FCSTD DOCUMENT  (FreeCAD 0.21R33694 (Git))
Label: kumiko_lattice_assembly
License: All rights reserved
LicenseURL: http://en.wikipedia.org/wiki/All_rights_reserved
objects: App::Link×9, App::Part×1
EXTERNAL_REF file=../master_kumiko_box.FCStd obj=Spreadsheet
EXTERNAL_REF file=../parts/kumiko/kumiko_strip_short.FCStd obj=Body052
EXTERNAL_REF file=../parts/kumiko/kumiko_strip_long.FCStd obj=Body053
EXTERNAL_REF file=../parts/kumiko/kumiko_strip_long_holes.FCStd obj=Body052
EXTERNAL_REF file=../parts/kumiko/kumiko_strip_short_holes.FCStd obj=Body052

FEATURE [App::Link] Link002  label="SpreadSheet"
  LinkedObject = -> <external ../master_kumiko_box.FCStd>#Spreadsheet
FEATURE [App::Link] Link003  label="short_strip_a"
  LinkPlacement = pos=(27.5,3,11) rot=(1,1,0;3.14159rad)
  LinkedObject = -> <external ../parts/kumiko/kumiko_strip_short.FCStd>#Body052
  Placement = pos=(27.5,3,11) rot=(1,1,0;3.14159rad)
  expr: .Placement.Base.x = <<SpreadSheet>>.kumiko_grid_size
  expr: .Placement.Base.y = <<SpreadSheet>>.kumiko_thickness
  expr: .Placement.Base.z = <<SpreadSheet>>.kumiko_hight
  expr: .Placement.Rotation.Angle = 180
  expr: .Placement.Rotation.Axis.x = 1
  expr: .Placement.Rotation.Axis.y = 1
  expr: .Placement.Rotation.Axis.z = 0
FEATURE [App::Link] Link004  label="short_strip_b"
  LinkPlacement = pos=(55,3,11) rot=(1,1,0;3.14159rad)
  LinkedObject = -> <external ../parts/kumiko/kumiko_strip_short.FCStd>#Body052
  Placement = pos=(55,3,11) rot=(1,1,0;3.14159rad)
  expr: .Placement.Base.x = <<SpreadSheet>>.kumiko_grid_size * 2
  expr: .Placement.Base.y = <<SpreadSheet>>.kumiko_thickness
  expr: .Placement.Base.z = <<SpreadSheet>>.kumiko_hight
  expr: .Placement.Rotation.Angle = 180
  expr: .Placement.Rotation.Axis.x = 1
  expr: .Placement.Rotation.Axis.y = 1
  expr: .Placement.Rotation.Axis.z = 0
FEATURE [App::Link] Link005  label="short_strip_c"
  LinkPlacement = pos=(82.5,3,11) rot=(1,1,0;3.14159rad)
  LinkedObject = -> <external ../parts/kumiko/kumiko_strip_short.FCStd>#Body052
  Placement = pos=(82.5,3,11) rot=(1,1,0;3.14159rad)
  expr: .Placement.Base.x = <<SpreadSheet>>.kumiko_grid_size * 3
  expr: .Placement.Base.y = <<SpreadSheet>>.kumiko_thickness
  expr: .Placement.Base.z = <<SpreadSheet>>.kumiko_hight
  expr: .Placement.Rotation.Angle = 180
  expr: .Placement.Rotation.Axis.x = 1
  expr: .Placement.Rotation.Axis.y = 1
  expr: .Placement.Rotation.Axis.z = 0
FEATURE [App::Link] Link009  label="strip_long_center"
  LinkPlacement = pos=(3,27.5,0) rot=(0,0,1;0rad)
  LinkedObject = -> <external ../parts/kumiko/kumiko_strip_long.FCStd>#Body053
  Placement = pos=(3,27.5,0) rot=(0,0,1;0rad)
  expr: .Placement.Base.x = <<SpreadSheet>>.kumiko_thickness
  expr: .Placement.Base.y = <<SpreadSheet>>.kumiko_grid_size
FEATURE [App::Link] Link  label="strip_long_front"
  LinkPlacement = pos=(3,0,0) rot=(0,0,1;0rad)
  LinkedObject = -> <external ../parts/kumiko/kumiko_strip_long_holes.FCStd>#Body052
  Placement = pos=(3,0,0) rot=(0,0,1;0rad)
  expr: .Placement.Base.x = <<SpreadSheet>>.kumiko_thickness
FEATURE [App::Link] Link010  label="strip_long_back"
  LinkPlacement = pos=(3,55,0) rot=(0,0,1;0rad)
  LinkedObject = -> <external ../parts/kumiko/kumiko_strip_long_holes.FCStd>#Body052
  Placement = pos=(3,55,0) rot=(0,0,1;0rad)
  expr: .Placement.Base.x = <<SpreadSheet>>.kumiko_thickness
  expr: .Placement.Base.y = <<SpreadSheet>>.kumiko_grid_size * 2
FEATURE [App::Link] Link011  label="short_strip_left"
  LinkPlacement = pos=(0,0,11) rot=(1,1,0;3.14159rad)
  LinkedObject = -> <external ../parts/kumiko/kumiko_strip_short_holes.FCStd>#Body052
  Placement = pos=(0,0,11) rot=(1,1,0;3.14159rad)
  expr: .Placement.Base.y = 0
  expr: .Placement.Base.z = <<SpreadSheet>>.kumiko_hight
FEATURE [App::Link] Link012  label="short_strip_right"
  LinkPlacement = pos=(110,0,11) rot=(1,1,0;3.14159rad)
  LinkedObject = -> <external ../parts/kumiko/kumiko_strip_short_holes.FCStd>#Body052
  Placement = pos=(110,0,11) rot=(1,1,0;3.14159rad)
  expr: .Placement.Base.x = <<SpreadSheet>>.kumiko_grid_size * 4
  expr: .Placement.Base.y = 0
  expr: .Placement.Base.z = <<SpreadSheet>>.kumiko_hight
FEATURE [App::Part] Part  label="lattice"
  Group = -> [Link005,Link,Link003,Link009,Link004,Link010,Link011,Link012]
  Origin = -> Origin

RESOLVED EXTERNAL PARTS (link-assembly join: the EXTERNAL_REF files above that resolve inside this repo's crawl, each included once):
---- part ../master_kumiko_box.FCStd = doc fcstd_d57fc246fb5e ----
FCSTD DOCUMENT  (FreeCAD 0.21R33771 (Git))
Label: master_kumiko_box
License: All rights reserved
LicenseURL: https://en.wikipedia.org/wiki/All_rights_reserved
objects: App::Link×3, App::Part×2, Spreadsheet::Sheet×1
EXTERNAL_REF file=assembly/box_assembly.FCStd obj=Part
EXTERNAL_REF file=assembly/lid_assembly.FCStd obj=Part
EXTERNAL_REF file=assembly/kumiko_assembly.FCStd obj=Part001

FEATURE [Spreadsheet::Sheet] Spreadsheet  label="SpreadSheet"
  cells = A1='name; B1='value; C1='calc (y/n); A2='box_length; B2(box_length)=130; C2='n; A3='box_width; B3(box_width)==B2 / 2 + B5 - B13 / 2; C3='n; A4='box_height; B4(box_height)=60; C4='y; A5='box_thickness; B5(box_thickness)=11.5; C5='y; A7='lid_height; B7(lid_height)==B8 * 17 / 8.5; C7='y; A8='lid_frame_width; B8(lid_frame_width)==B5 - B13; C8='y; A9='lid_lip_width; B9(lid_lip_width)==B5 - B8; C9='y; A10='lid_lip_height; B10(lid_lip_hight)=3; C10='y; A12='kumiko_hight; B12(kumiko_hight)==B7 * 11 / 17; C12='y; A13='kumiko_thickness; B13(kumiko_thickness)=3; C13='n; A14='kumiko_grid_size; B14(kumiko_grid_size)==(B2 - 2 * B8 - B13) / 4; C14='y; A16='box_wall_height; B16(box_wall_height)==B4 - B7 - B18; C16='y; A18='floor_edge; B18(floor_edge)=2; C18='n; A20='cnc_spacing; B20(cnc_spacing)=0; C20='y
FEATURE [App::Link] Link  label="box"
  LinkedObject = -> <external assembly/box_assembly.FCStd>#Part
FEATURE [App::Link] Link001  label="lid"
  LinkPlacement = pos=(0,0,43) rot=(0,0,1;0rad)
  LinkedObject = -> <external assembly/lid_assembly.FCStd>#Part
  Placement = pos=(0,0,43) rot=(0,0,1;0rad)
  expr: .Placement.Base.z = <<SpreadSheet>>.box_height - <<SpreadSheet>>.lid_height
FEATURE [App::Link] Link002  label="kumiko_assembly"
  LinkPlacement = pos=(8.5,8.5,49) rot=(0,0,1;0rad)
  LinkedObject = -> <external assembly/kumiko_assembly.FCStd>#Part001
  Placement = pos=(8.5,8.5,49) rot=(0,0,1;0rad)
  expr: .Placement.Base.x = <<SpreadSheet>>.lid_frame_width
  expr: .Placement.Base.y = <<SpreadSheet>>.lid_frame_width
  expr: .Placement.Base.z = <<SpreadSheet>>.box_height - Spreadsheet.kumiko_hight
FEATURE [App::Part] Part  label="lid_complete"
  Group = -> [Link002,Link001]
  Origin = -> Origin
FEATURE [App::Part] Part001  label="kumiko_box_complete"
  Group = -> [Part,Link]
  Origin = -> Origin001
---- part ../parts/kumiko/kumiko_strip_long.FCStd = doc fcstd_fbc0481b5c11 ----
FCSTD DOCUMENT  (FreeCAD 0.21R33694 (Git))
Label: kumiko_strip_long
License: All rights reserved
LicenseURL: https://en.wikipedia.org/wiki/All_rights_reserved
objects: Sketcher::SketchObject×3, PartDesign::Pad×2, PartDesign::LinearPattern×2, App::Link×1, PartDesign::Pocket×1, PartDesign::Body×1
note: 12 computed .brp shape members not serialized (recipe doc carries the construction recipe); baked Part::Feature solids carry a one-line shape summary decoded from their .brp
EXTERNAL_REF file=../../master_kumiko_box.FCStd obj=Spreadsheet

FEATURE [App::Link] Link  label="SpreadSheet"
  LinkedObject = -> <external ../../master_kumiko_box.FCStd>#Spreadsheet
FEATURE [Sketcher::SketchObject] Sketch081  label="strip_profile_drawing001"
  FullyConstrained = true
  MapMode = 5
  Placement = pos=(0,0,0) rot=(0.57735,0.57735,0.57735;2.0944rad)
  Support = -> [YZ_Plane071]
  expr: Constraints[10] = 0
  expr: Constraints[8] = <<SpreadSheet>>.kumiko_thickness
  expr: Constraints[9] = <<SpreadSheet>>.kumiko_hight
  sketch-geometry (4):
    g0: LineSegment StartX=0 StartY=11 StartZ=0 EndX=3 EndY=11 EndZ=0
    g1: LineSegment StartX=3 StartY=11 StartZ=0 EndX=3 EndY=0 EndZ=0
    g2: LineSegment StartX=3 StartY=0 StartZ=0 EndX=0 EndY=0 EndZ=0
    g3: LineSegment StartX=0 StartY=0 StartZ=0 EndX=0 EndY=11 EndZ=0
  constraints (12):
    c: Coincident(g0,g1)
    c: Coincident(g1,g2)
    c: Coincident(g2,g3)
    c: Coincident(g3,g0)
    c: Horizontal(g0)
    c: Horizontal(g2)
    c: Vertical(g1)
    c: Vertical(g3)
    c: DistanceX(g0,g0) = 3
    c: DistanceY(g3,g3) = 11
    c: DistanceX(g0,g-1) = 0
    c: DistanceY(g-1,g2) = 0
FEATURE [PartDesign::Pad] Pad038  label="strip_extrusion001"
  Direction = (1,-2e-16,3e-16)
  Length = 107
  Length2 = 10
  Placement = pos=(0,0,0) rot=(0.57735,0.57735,0.57735;2.0944rad)
  Profile = -> Sketch081
  ReferenceAxis = -> Sketch081 [N_Axis]
  Type = 0
  expr: Length = <<SpreadSheet>>.box_length - 2 * <<SpreadSheet>>.lid_frame_width - 2 * <<SpreadSheet>>.kumiko_thickness
FEATURE [Sketcher::SketchObject] Sketch
  FullyConstrained = true
  MapMode = 5
  Placement = pos=(107,-2.35e-14,2.35e-14) rot=(0.57735,0.57735,0.57735;2.0944rad)
  Support = -> [Pad038]
  expr: Constraints[0] = <<SpreadSheet>>.kumiko_thickness / 2
  expr: Constraints[12] = <<SpreadSheet>>.kumiko_thickness
  expr: Constraints[1] = <<SpreadSheet>>.kumiko_hight / 2
  sketch-geometry (5):
    g0: GeomPoint X=1.5 Y=5.5 Z=0
    g1: LineSegment StartX=0 StartY=7 StartZ=0 EndX=3 EndY=7 EndZ=0
    g2: LineSegment StartX=3 StartY=7 StartZ=0 EndX=3 EndY=4 EndZ=0
    g3: LineSegment StartX=3 StartY=4 StartZ=0 EndX=0 EndY=4 EndZ=0
    g4: LineSegment StartX=0 StartY=4 StartZ=0 EndX=0 EndY=7 EndZ=0
  constraints (13):
    c: DistanceX(g-1,g0) = 1.5
    c: DistanceY(g-1,g0) = 5.5
    c: Coincident(g1,g2)
    c: Coincident(g2,g3)
    c: Coincident(g3,g4)
    c: Coincident(g4,g1)
    c: Horizontal(g1)
    c: Horizontal(g3)
    c: Vertical(g2)
    c: Vertical(g4)
    c: Symmetric(g1,g2,g0)
    c: Equal(g4,g1)
    c: DistanceY(g2,g2) = 3
FEATURE [PartDesign::Pad] Pad
  BaseFeature = -> Pad038
  Direction = (1,-4e-16,4e-16)
  Length = 6
  Length2 = 10
  Placement = pos=(0,0,0) rot=(0.57735,0.57735,0.57735;2.0944rad)
  Profile = -> Sketch
  ReferenceAxis = -> Sketch [N_Axis]
  Type = 0
  expr: Length = <<SpreadSheet>>.kumiko_thickness * 2
FEATURE [PartDesign::LinearPattern] LinearPattern001
  BaseFeature = -> Pad
  Direction = -> X_Axis071
  Length = 113
  Occurrences = 2
  Originals = -> [Pad]
  Placement = pos=(0,0,0) rot=(0.57735,0.57735,0.57735;2.0944rad)
  Reversed = true
  expr: Length = <<SpreadSheet>>.box_length - 2 * <<SpreadSheet>>.lid_frame_width
FEATURE [Sketcher::SketchObject] Sketch082
  FullyConstrained = true
  MapMode = 5
  Placement = pos=(0,0,0) rot=(-0.57735,-0.57735,0.57735;4.18879rad)
  Support = -> [LinearPattern001]
  expr: Constraints[0] = <<SpreadSheet>>.kumiko_hight / 2
  expr: Constraints[10] = <<SpreadSheet>>.kumiko_thickness
  expr: Constraints[12] = -<<SpreadSheet>>.kumiko_hight / 2
  expr: Constraints[1] = <<SpreadSheet>>.kumiko_grid_size - <<SpreadSheet>>.kumiko_thickness / 2
  sketch-geometry (5):
    g0: GeomPoint X=-5.5 Y=26 Z=0
    g1: LineSegment StartX=-5.5 StartY=27.5 StartZ=0 EndX=-11 EndY=27.5 EndZ=0
    g2: LineSegment StartX=-11 StartY=27.5 StartZ=0 EndX=-11 EndY=24.5 EndZ=0
    g3: LineSegment StartX=-11 StartY=24.5 StartZ=0 EndX=-5.5 EndY=24.5 EndZ=0
    g4: LineSegment StartX=-5.5 StartY=24.5 StartZ=0 EndX=-5.5 EndY=27.5 EndZ=0
  constraints (13):
    c: DistanceX(g0,g-1) = 5.5
    c: DistanceY(g-1,g0) = 26
    c: Coincident(g1,g2)
    c: Coincident(g2,g3)
    c: Coincident(g3,g4)
    c: Coincident(g4,g1)
    c: Horizontal(g1)
    c: Horizontal(g3)
    c: Vertical(g2)
    c: Vertical(g4)
    c: DistanceY(g2,g2) = 3
    c: Symmetric(g1,g3,g0)
    c: DistanceX(g1,g1) = -5.5
FEATURE [PartDesign::Pocket] Pocket
  BaseFeature = -> LinearPattern001
  Direction = (7e-16,1,-4e-16)
  Length = 3
  Length2 = 5
  Placement = pos=(0,0,0) rot=(0.57735,0.57735,0.57735;2.0944rad)
  Profile = -> Sketch082
  ReferenceAxis = -> Sketch082 [N_Axis]
  Type = 0
  expr: Length = <<SpreadSheet>>.kumiko_thickness
FEATURE [PartDesign::LinearPattern] LinearPattern002
  BaseFeature = -> Pocket
  Direction = -> X_Axis071
  Length = 55
  Occurrences = 3
  Originals = -> [Pocket]
  Placement = pos=(0,0,0) rot=(0.57735,0.57735,0.57735;2.0944rad)
  expr: Length = <<SpreadSheet>>.kumiko_grid_size * 2
FEATURE [PartDesign::Body] Body053  label="strip_long_body001"
  Group = -> [Sketch081,Pad038,Sketch,Pad,LinearPattern001,Sketch082,Pocket,LinearPattern002]
  Origin = -> Origin071
  Tip = -> LinearPattern002
  expr: .Placement.Base.x = 0
  expr: .Placement.Base.y = 0
  expr: .Placement.Base.z = 0
---- part ../parts/kumiko/kumiko_strip_long_holes.FCStd = doc fcstd_25b771c1c85f ----
FCSTD DOCUMENT  (FreeCAD 0.21R33694 (Git))
Label: kumiko_strip_long_holes
License: All rights reserved
LicenseURL: http://en.wikipedia.org/wiki/All_rights_reserved
objects: Sketcher::SketchObject×3, PartDesign::Pad×2, PartDesign::LinearPattern×2, App::Link×1, PartDesign::Pocket×1, PartDesign::Body×1
note: 12 computed .brp shape members not serialized (recipe doc carries the construction recipe); baked Part::Feature solids carry a one-line shape summary decoded from their .brp
EXTERNAL_REF file=../../master_kumiko_box.FCStd obj=Spreadsheet

FEATURE [App::Link] Link  label="SpreadSheet"
  LinkedObject = -> <external ../../master_kumiko_box.FCStd>#Spreadsheet
FEATURE [Sketcher::SketchObject] Sketch079  label="strip_profile_drawing"
  FullyConstrained = true
  MapMode = 5
  Placement = pos=(0,0,0) rot=(0.57735,0.57735,0.57735;2.0944rad)
  Support = -> [YZ_Plane070]
  expr: Constraints[10] = 0
  expr: Constraints[8] = <<SpreadSheet>>.kumiko_thickness
  expr: Constraints[9] = <<SpreadSheet>>.kumiko_hight
  sketch-geometry (4):
    g0: LineSegment StartX=0 StartY=11 StartZ=0 EndX=3 EndY=11 EndZ=0
    g1: LineSegment StartX=3 StartY=11 StartZ=0 EndX=3 EndY=0 EndZ=0
    g2: LineSegment StartX=3 StartY=0 StartZ=0 EndX=0 EndY=0 EndZ=0
    g3: LineSegment StartX=0 StartY=0 StartZ=0 EndX=0 EndY=11 EndZ=0
  constraints (12):
    c: Coincident(g0,g1)
    c: Coincident(g1,g2)
    c: Coincident(g2,g3)
    c: Coincident(g3,g0)
    c: Horizontal(g0)
    c: Horizontal(g2)
    c: Vertical(g1)
    c: Vertical(g3)
    c: DistanceX(g0,g0) = 3
    c: DistanceY(g3,g3) = 11
    c: DistanceX(g0,g-1) = 0
    c: DistanceY(g-1,g2) = 0
FEATURE [PartDesign::Pad] Pad037  label="strip_extrusion"
  Direction = (1,-2e-16,3e-16)
  Length = 107
  Length2 = 10
  Placement = pos=(0,0,0) rot=(0.57735,0.57735,0.57735;2.0944rad)
  Profile = -> Sketch079
  ReferenceAxis = -> Sketch079 [N_Axis]
  Type = 0
  expr: Length = <<SpreadSheet>>.box_length - 2 * <<SpreadSheet>>.lid_frame_width - 2 * <<SpreadSheet>>.kumiko_thickness
FEATURE [Sketcher::SketchObject] Sketch
  FullyConstrained = true
  MapMode = 5
  Placement = pos=(107,-2.35e-14,2.35e-14) rot=(0.57735,0.57735,0.57735;2.0944rad)
  Support = -> [Pad037]
  expr: Constraints[0] = <<SpreadSheet>>.kumiko_thickness / 2
  expr: Constraints[12] = <<SpreadSheet>>.kumiko_thickness
  expr: Constraints[1] = <<SpreadSheet>>.kumiko_hight / 2
  sketch-geometry (5):
    g0: GeomPoint X=1.5 Y=5.5 Z=0
    g1: LineSegment StartX=0 StartY=7 StartZ=0 EndX=3 EndY=7 EndZ=0
    g2: LineSegment StartX=3 StartY=7 StartZ=0 EndX=3 EndY=4 EndZ=0
    g3: LineSegment StartX=3 StartY=4 StartZ=0 EndX=0 EndY=4 EndZ=0
    g4: LineSegment StartX=0 StartY=4 StartZ=0 EndX=0 EndY=7 EndZ=0
  constraints (13):
    c: DistanceX(g-1,g0) = 1.5
    c: DistanceY(g-1,g0) = 5.5
    c: Coincident(g1,g2)
    c: Coincident(g2,g3)
    c: Coincident(g3,g4)
    c: Coincident(g4,g1)
    c: Horizontal(g1)
    c: Horizontal(g3)
    c: Vertical(g2)
    c: Vertical(g4)
    c: Symmetric(g1,g2,g0)
    c: Equal(g4,g1)
    c: DistanceY(g2,g2) = 3
FEATURE [PartDesign::Pad] Pad
  BaseFeature = -> Pad037
  Direction = (1,-4e-16,4e-16)
  Length = 3
  Length2 = 10
  Placement = pos=(0,0,0) rot=(0.57735,0.57735,0.57735;2.0944rad)
  Profile = -> Sketch
  ReferenceAxis = -> Sketch [N_Axis]
  Type = 0
  expr: Length = <<SpreadSheet>>.kumiko_thickness
FEATURE [PartDesign::LinearPattern] LinearPattern
  BaseFeature = -> Pad
  Direction = -> X_Axis070
  Length = 110
  Occurrences = 2
  Originals = -> [Pad]
  Placement = pos=(0,0,0) rot=(0.57735,0.57735,0.57735;2.0944rad)
  Reversed = true
  expr: Length = <<SpreadSheet>>.box_length - 2 * <<SpreadSheet>>.lid_frame_width - <<SpreadSheet>>.kumiko_thickness
FEATURE [Sketcher::SketchObject] Sketch080
  FullyConstrained = true
  MapMode = 5
  Placement = pos=(0,0,0) rot=(-0.57735,-0.57735,0.57735;4.18879rad)
  Support = -> [LinearPattern]
  expr: Constraints[0] = <<SpreadSheet>>.kumiko_hight / 2
  expr: Constraints[12] = <<SpreadSheet>>.kumiko_thickness
  expr: Constraints[1] = <<SpreadSheet>>.kumiko_grid_size - <<SpreadSheet>>.kumiko_thickness / 2
  sketch-geometry (5):
    g0: GeomPoint X=-5.5 Y=26 Z=0
    g1: LineSegment StartX=-7 StartY=27.5 StartZ=0 EndX=-4 EndY=27.5 EndZ=0
    g2: LineSegment StartX=-4 StartY=27.5 StartZ=0 EndX=-4 EndY=24.5 EndZ=0
    g3: LineSegment StartX=-4 StartY=24.5 StartZ=0 EndX=-7 EndY=24.5 EndZ=0
    g4: LineSegment StartX=-7 StartY=24.5 StartZ=0 EndX=-7 EndY=27.5 EndZ=0
  constraints (13):
    c: DistanceX(g0,g-1) = 5.5
    c: DistanceY(g-1,g0) = 26
    c: Coincident(g1,g2)
    c: Coincident(g2,g3)
    c: Coincident(g3,g4)
    c: Coincident(g4,g1)
    c: Horizontal(g1)
    c: Horizontal(g3)
    c: Vertical(g2)
    c: Vertical(g4)
    c: Symmetric(g1,g2,g0)
    c: Equal(g1,g4)
    c: DistanceY(g2,g2) = 3
FEATURE [PartDesign::Pocket] Pocket
  BaseFeature = -> LinearPattern
  Direction = (7e-16,1,-4e-16)
  Length = 3
  Length2 = 5
  Placement = pos=(0,0,0) rot=(0.57735,0.57735,0.57735;2.0944rad)
  Profile = -> Sketch080
  ReferenceAxis = -> Sketch080 [N_Axis]
  Type = 0
  expr: Length = <<SpreadSheet>>.kumiko_thickness
FEATURE [PartDesign::LinearPattern] LinearPattern001
  BaseFeature = -> Pocket
  Direction = -> X_Axis070
  Length = 55
  Occurrences = 3
  Originals = -> [Pocket]
  Placement = pos=(0,0,0) rot=(0.57735,0.57735,0.57735;2.0944rad)
  expr: Length = <<SpreadSheet>>.kumiko_grid_size * 2
FEATURE [PartDesign::Body] Body052  label="strip_long_body"
  Group = -> [Sketch079,Pad037,Sketch,Pad,LinearPattern,Sketch080,Pocket,LinearPattern001]
  Origin = -> Origin070
  Tip = -> LinearPattern001
  expr: .Placement.Base.x = 0
  expr: .Placement.Base.y = 0
  expr: .Placement.Base.z = 0
---- part ../parts/kumiko/kumiko_strip_short.FCStd = doc fcstd_705df1ea343c ----
FCSTD DOCUMENT  (FreeCAD 0.21R33694 (Git))
Label: kumiko_strip_short
License: All rights reserved
LicenseURL: https://en.wikipedia.org/wiki/All_rights_reserved
objects: Sketcher::SketchObject×3, PartDesign::Pad×2, PartDesign::Pocket×1, App::Link×1, PartDesign::LinearPattern×1, PartDesign::Body×1
note: 11 computed .brp shape members not serialized (recipe doc carries the construction recipe); baked Part::Feature solids carry a one-line shape summary decoded from their .brp
EXTERNAL_REF file=../../master_kumiko_box.FCStd obj=Spreadsheet

FEATURE [Sketcher::SketchObject] Sketch079  label="short_strip_profile"
  FullyConstrained = true
  MapMode = 5
  Placement = pos=(0,0,0) rot=(0.57735,0.57735,0.57735;2.0944rad)
  Support = -> [YZ_Plane070]
  expr: Constraints[10] = 0
  expr: Constraints[8] = <<SpreadSheet>>.kumiko_thickness
  expr: Constraints[9] = <<SpreadSheet>>.kumiko_hight
  sketch-geometry (4):
    g0: LineSegment StartX=0 StartY=11 StartZ=0 EndX=3 EndY=11 EndZ=0
    g1: LineSegment StartX=3 StartY=11 StartZ=0 EndX=3 EndY=0 EndZ=0
    g2: LineSegment StartX=3 StartY=0 StartZ=0 EndX=0 EndY=0 EndZ=0
    g3: LineSegment StartX=0 StartY=0 StartZ=0 EndX=0 EndY=11 EndZ=0
  constraints (12):
    c: Coincident(g0,g1)
    c: Coincident(g1,g2)
    c: Coincident(g2,g3)
    c: Coincident(g3,g0)
    c: Horizontal(g0)
    c: Horizontal(g2)
    c: Vertical(g1)
    c: Vertical(g3)
    c: DistanceX(g0,g0) = 3
    c: DistanceY(g3,g3) = 11
    c: DistanceX(g0,g-1) = 0
    c: DistanceY(g-1,g2) = 0
FEATURE [PartDesign::Pad] Pad037  label="short_strip_extrusion"
  Direction = (1,-2e-16,3e-16)
  Length = 52
  Length2 = 10
  Placement = pos=(0,0,0) rot=(0.57735,0.57735,0.57735;2.0944rad)
  Profile = -> Sketch079
  ReferenceAxis = -> Sketch079 [N_Axis]
  Type = 0
  expr: Length = <<SpreadSheet>>.box_width - 2 * <<SpreadSheet>>.lid_frame_width - 2 * <<SpreadSheet>>.kumiko_thickness
FEATURE [Sketcher::SketchObject] Sketch080  label="half_lap_drawing"
  FullyConstrained = true
  MapMode = 5
  Placement = pos=(0,0,0) rot=(-0.57735,-0.57735,0.57735;4.18879rad)
  Support = -> [Pad037]
  expr: Constraints[10] = (<<SpreadSheet>>.box_width - 2 * <<SpreadSheet>>.lid_frame_width - <<SpreadSheet>>.kumiko_thickness - 2 * <<SpreadSheet>>.kumiko_thickness) / 2
  expr: Constraints[11] = <<SpreadSheet>>.kumiko_hight / 2
  expr: Constraints[8] = <<SpreadSheet>>.kumiko_thickness
  expr: Constraints[9] = <<SpreadSheet>>.kumiko_hight / 2
  sketch-geometry (4):
    g0: LineSegment StartX=-11 StartY=24.5 StartZ=0 EndX=-5.5 EndY=24.5 EndZ=0
    g1: LineSegment StartX=-5.5 StartY=24.5 StartZ=0 EndX=-5.5 EndY=27.5 EndZ=0
    g2: LineSegment StartX=-5.5 StartY=27.5 StartZ=0 EndX=-11 EndY=27.5 EndZ=0
    g3: LineSegment StartX=-11 StartY=27.5 StartZ=0 EndX=-11 EndY=24.5 EndZ=0
  constraints (12):
    c: Coincident(g0,g1)
    c: Coincident(g1,g2)
    c: Coincident(g2,g3)
    c: Coincident(g3,g0)
    c: Horizontal(g0)
    c: Horizontal(g2)
    c: Vertical(g1)
    c: Vertical(g3)
    c: DistanceY(g1,g1) = 3
    c: DistanceX(g0,g0) = 5.5
    c: DistanceY(g-1,g0) = 24.5
    c: DistanceX(g0,g-1) = 5.5
FEATURE [PartDesign::Pocket] Pocket019  label="half_lap_joint"
  BaseFeature = -> Pad037
  Direction = (4e-16,1,-2e-16)
  Length = 3
  Length2 = 5
  Placement = pos=(0,0,0) rot=(0.57735,0.57735,0.57735;2.0944rad)
  Profile = -> Sketch080
  ReferenceAxis = -> Sketch080 [N_Axis]
  Type = 0
  expr: Length = <<SpreadSheet>>.kumiko_thickness
FEATURE [App::Link] Link  label="SpreadSheet"
  LinkedObject = -> <external ../../master_kumiko_box.FCStd>#Spreadsheet
FEATURE [Sketcher::SketchObject] Sketch
  FullyConstrained = true
  MapMode = 5
  Placement = pos=(52,-1.14e-14,1.14e-14) rot=(0.57735,0.57735,0.57735;2.0944rad)
  Support = -> [Pocket019]
  expr: Constraints[11] = <<SpreadSheet>>.kumiko_thickness
  expr: Constraints[8] = <<SpreadSheet>>.kumiko_thickness / 2
  expr: Constraints[9] = <<SpreadSheet>>.kumiko_hight / 2
  sketch-geometry (5):
    g0: LineSegment StartX=0 StartY=4 StartZ=0 EndX=3 EndY=4 EndZ=0
    g1: LineSegment StartX=3 StartY=4 StartZ=0 EndX=3 EndY=7 EndZ=0
    g2: LineSegment StartX=3 StartY=7 StartZ=0 EndX=0 EndY=7 EndZ=0
    g3: LineSegment StartX=0 StartY=7 StartZ=0 EndX=0 EndY=4 EndZ=0
    g4: GeomPoint X=1.5 Y=5.5 Z=0
  constraints (13):
    c: Coincident(g0,g1)
    c: Coincident(g1,g2)
    c: Coincident(g2,g3)
    c: Coincident(g3,g0)
    c: Horizontal(g0)
    c: Horizontal(g2)
    c: Vertical(g1)
    c: Vertical(g3)
    c: DistanceX(g-1,g4) = 1.5
    c: DistanceY(g-1,g4) = 5.5
    c: Symmetric(g0,g1,g4)
    c: DistanceX(g0,g0) = 3
    c: Equal(g0,g3)
FEATURE [PartDesign::Pad] Pad
  BaseFeature = -> Pocket019
  Direction = (1,-9e-16,6e-16)
  Length = 6
  Length2 = 10
  Placement = pos=(0,0,0) rot=(0.57735,0.57735,0.57735;2.0944rad)
  Profile = -> Sketch
  ReferenceAxis = -> Sketch [N_Axis]
  Type = 0
  expr: Length = 2 * <<SpreadSheet>>.kumiko_thickness
FEATURE [PartDesign::LinearPattern] LinearPattern
  BaseFeature = -> Pad
  Direction = -> X_Axis070
  Length = 58
  Occurrences = 2
  Originals = -> [Pad]
  Placement = pos=(0,0,0) rot=(0.57735,0.57735,0.57735;2.0944rad)
  Reversed = true
  expr: Length = <<SpreadSheet>>.box_width - 2 * <<SpreadSheet>>.lid_frame_width
FEATURE [PartDesign::Body] Body052  label="short_strip_body"
  Group = -> [Sketch079,Pad037,Sketch080,Pocket019,Sketch,Pad,LinearPattern]
  Origin = -> Origin070
  Tip = -> LinearPattern
  expr: .Placement.Base.x = 0
  expr: .Placement.Base.y = 0
  expr: .Placement.Base.z = 0
---- part ../parts/kumiko/kumiko_strip_short_holes.FCStd = doc fcstd_b76901bbe5f5 ----
FCSTD DOCUMENT  (FreeCAD 0.21R33694 (Git))
Label: kumiko_strip_short_holes
License: All rights reserved
LicenseURL: http://en.wikipedia.org/wiki/All_rights_reserved
objects: Sketcher::SketchObject×2, PartDesign::Pad×1, PartDesign::Pocket×1, App::Link×1, PartDesign::LinearPattern×1, PartDesign::Body×1
note: 8 computed .brp shape members not serialized (recipe doc carries the construction recipe); baked Part::Feature solids carry a one-line shape summary decoded from their .brp
EXTERNAL_REF file=../../master_kumiko_box.FCStd obj=Spreadsheet

FEATURE [Sketcher::SketchObject] Sketch079  label="short_strip_profile"
  FullyConstrained = true
  MapMode = 5
  Placement = pos=(0,0,0) rot=(0.57735,0.57735,0.57735;2.0944rad)
  Support = -> [YZ_Plane070]
  expr: Constraints[10] = 0
  expr: Constraints[8] = <<SpreadSheet>>.kumiko_thickness
  expr: Constraints[9] = <<SpreadSheet>>.kumiko_hight
  sketch-geometry (4):
    g0: LineSegment StartX=0 StartY=11 StartZ=0 EndX=3 EndY=11 EndZ=0
    g1: LineSegment StartX=3 StartY=11 StartZ=0 EndX=3 EndY=0 EndZ=0
    g2: LineSegment StartX=3 StartY=0 StartZ=0 EndX=0 EndY=0 EndZ=0
    g3: LineSegment StartX=0 StartY=0 StartZ=0 EndX=0 EndY=11 EndZ=0
  constraints (12):
    c: Coincident(g0,g1)
    c: Coincident(g1,g2)
    c: Coincident(g2,g3)
    c: Coincident(g3,g0)
    c: Horizontal(g0)
    c: Horizontal(g2)
    c: Vertical(g1)
    c: Vertical(g3)
    c: DistanceX(g0,g0) = 3
    c: DistanceY(g3,g3) = 11
    c: DistanceX(g0,g-1) = 0
    c: DistanceY(g-1,g2) = 0
FEATURE [PartDesign::Pad] Pad037  label="short_strip_extrusion"
  Direction = (1,-2e-16,3e-16)
  Length = 58
  Length2 = 10
  Placement = pos=(0,0,0) rot=(0.57735,0.57735,0.57735;2.0944rad)
  Profile = -> Sketch079
  ReferenceAxis = -> Sketch079 [N_Axis]
  Type = 0
  expr: Length = <<SpreadSheet>>.box_width - 2 * <<SpreadSheet>>.lid_frame_width
FEATURE [Sketcher::SketchObject] Sketch080  label="half_lap_drawing"
  FullyConstrained = true
  MapMode = 5
  Placement = pos=(0,0,0) rot=(-0.57735,-0.57735,0.57735;4.18879rad)
  Support = -> [Pad037]
  expr: Constraints[10] = 0
  expr: Constraints[11] = (<<SpreadSheet>>.kumiko_hight - <<SpreadSheet>>.kumiko_thickness) / 2
  expr: Constraints[8] = <<SpreadSheet>>.kumiko_thickness
  expr: Constraints[9] = <<SpreadSheet>>.kumiko_thickness
  sketch-geometry (4):
    g0: LineSegment StartX=-7 StartY=0 StartZ=0 EndX=-4 EndY=0 EndZ=0
    g1: LineSegment StartX=-4 StartY=0 StartZ=0 EndX=-4 EndY=3 EndZ=0
    g2: LineSegment StartX=-4 StartY=3 StartZ=0 EndX=-7 EndY=3 EndZ=0
    g3: LineSegment StartX=-7 StartY=3 StartZ=0 EndX=-7 EndY=0 EndZ=0
  constraints (12):
    c: Coincident(g0,g1)
    c: Coincident(g1,g2)
    c: Coincident(g2,g3)
    c: Coincident(g3,g0)
    c: Horizontal(g0)
    c: Horizontal(g2)
    c: Vertical(g1)
    c: Vertical(g3)
    c: DistanceY(g1,g1) = 3
    c: DistanceX(g0,g0) = 3
    c: DistanceY(g-1,g0) = 0
    c: DistanceX(g0,g-1) = 4
FEATURE [PartDesign::Pocket] Pocket019  label="half_lap_joint"
  BaseFeature = -> Pad037
  Direction = (4e-16,1,-2e-16)
  Length = 3
  Length2 = 5
  Placement = pos=(0,0,0) rot=(0.57735,0.57735,0.57735;2.0944rad)
  Profile = -> Sketch080
  ReferenceAxis = -> Sketch080 [N_Axis]
  Type = 0
  expr: Length = <<SpreadSheet>>.kumiko_thickness
FEATURE [App::Link] Link  label="SpreadSheet"
  LinkedObject = -> <external ../../master_kumiko_box.FCStd>#Spreadsheet
FEATURE [PartDesign::LinearPattern] LinearPattern
  BaseFeature = -> Pocket019
  Direction = -> X_Axis070
  Length = 55
  Occurrences = 3
  Originals = -> [Pocket019]
  Placement = pos=(0,0,0) rot=(0.57735,0.57735,0.57735;2.0944rad)
  expr: Length = <<SpreadSheet>>.kumiko_grid_size * 2
FEATURE [PartDesign::Body] Body052  label="short_strip_body"
  Group = -> [Sketch079,Pad037,Sketch080,Pocket019,LinearPattern]
  Origin = -> Origin070
  Tip = -> LinearPattern
  expr: .Placement.Base.x = 0
  expr: .Placement.Base.y = 0
  expr: .Placement.Base.z = 0
